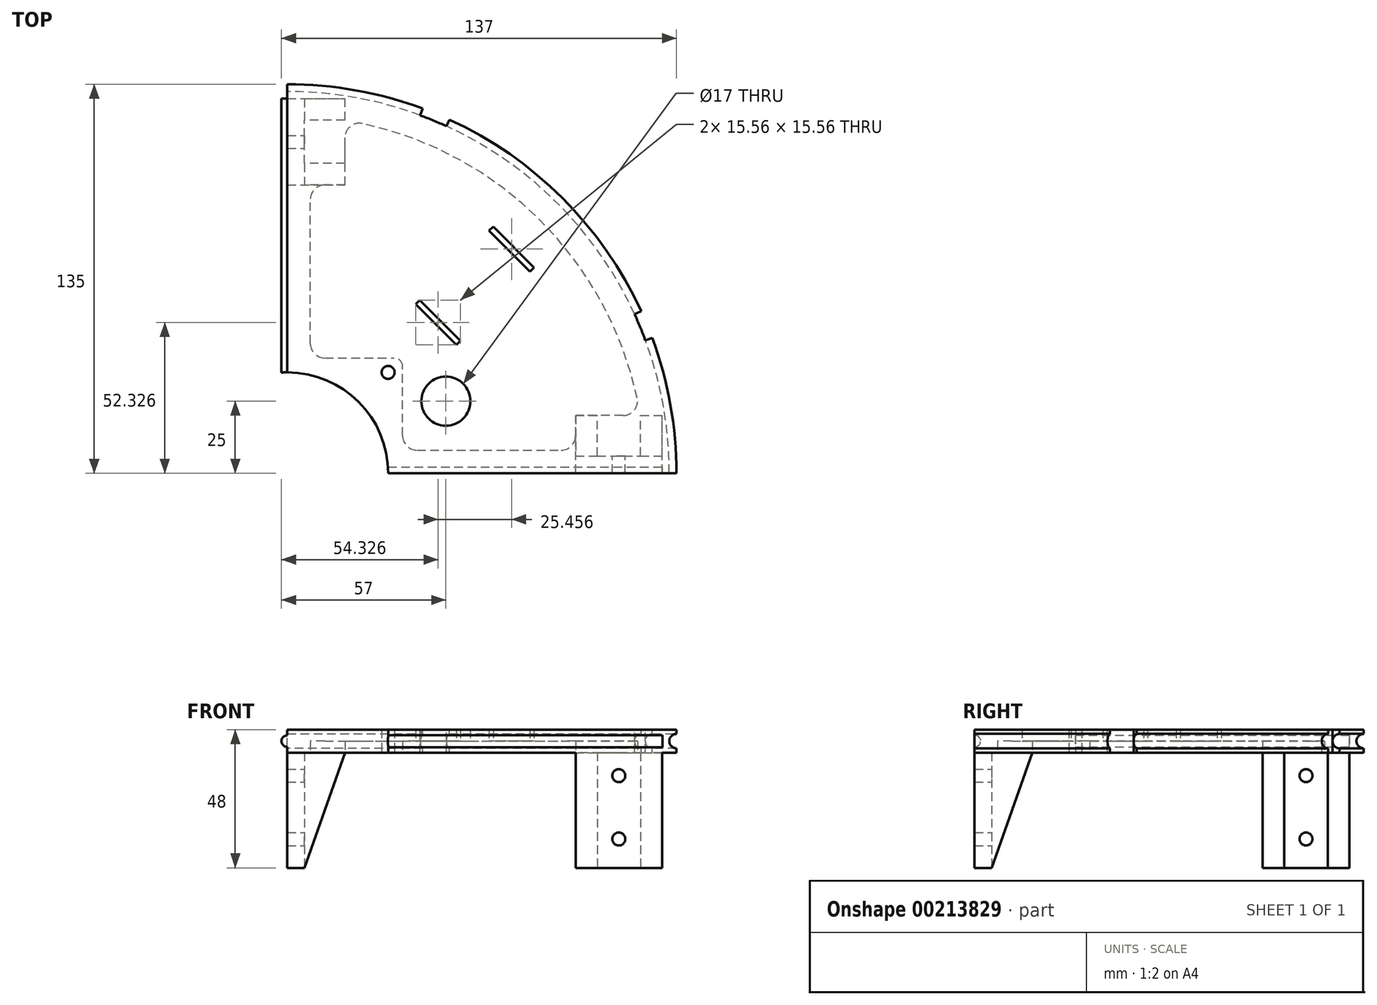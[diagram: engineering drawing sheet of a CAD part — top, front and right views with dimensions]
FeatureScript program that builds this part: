
annotation { "Feature Type Name" : "Feature", "Feature Type Description" : "" }
export const myFeature = defineFeature(function(context is Context, id is Id, definition is map)
    precondition{}
    {
        {
            var Q0;
            Q0=qCreatedBy(makeId("Top.planeOp"),FACE);
            var sketch = newSketch(context, id + "F0", { "sketchPlane" : qUnion([Q0])});
            skArc(sketch, "E0", {"start": v(135, 0) * mm, "mid": v(95.46, 95.46) * mm, "end": v(0, 135) * mm});
            skArc(sketch, "E1", {"start": v(35, 0) * mm, "mid": v(24.75, 24.75) * mm, "end": v(0, 35) * mm});
            skLineSegment(sketch, "E2.trimOffspring", {"start": v(35, 0) * mm, "end": v(135, 0) * mm});
            skLineSegment(sketch, "E3.1.5", {"start": v(0, 35) * mm, "end": v(0, 135) * mm});
            skCircle(sketch, "E4", {"center": v(35, 35) * mm, "radius": 2.25 * mm});
            skSolve(sketch);
        }
        {
            var Q0;
            Q0 = qSketchRegion(id + "F0", true);
            extrude(context, id + "F1", {"entities" : qUnion([Q0]), "depth" : 8 * mm});
        }
        {
            var Q0;
            Q0=qCreatedBy(makeId("Top.planeOp"),FACE);
            cPlane(context, id + "F2", {"entities" : qUnion([Q0]), "cplaneType" : CPlaneType.OFFSET, "offset" : 4 * mm, "width" : 150 * mm, "height" : 150 * mm});
        }
        {
            var Q0;
            Q0=qCreatedBy(id+"F2.planeOp",FACE);
            var sketch = newSketch(context, id + "F3", { "sketchPlane" : qUnion([Q0])});
            skCircle(sketch, "E5", {"center": v(0, 0) * mm, "radius": 135 * mm});
            skSolve(sketch);
        }
        {
            var Q0;
            Q0=makeQuery(id+"F1.opExtrude","SWEPT_FACE",FACE,{"disambiguationData":[OSD([sQuery(id+"F0.wireOp",EDGE,"E2.trimOffspring")])]});
            var sketch = newSketch(context, id + "F4", { "sketchPlane" : qUnion([Q0])});
            skCircle(sketch, "E6", {"center": v(135, 4) * mm, "radius": 2.5 * mm});
            skSolve(sketch);
        }
        {
            var Q0;
            Q0 = qSketchRegion(id + "F4", true);
            var Q1;
            Q1 = qConstructionFilter(qBodyType(qCreatedBy(id + "F3" ,EDGE), BodyType.WIRE), ConstructionObject.NO);
            sweep(context, id + "F5", {"operationType" : NewBodyOperationType.REMOVE, "profiles" : qUnion([Q0]), "path" : qUnion([Q1])});
        }
        {
            var Q0;
            Q0=makeQuery(id+"F1.opExtrude","CAP_FACE",FACE,{"disambiguationData":[OSD([sQuery(id+"F0.wireOp",EDGE,"E0"),sQuery(id+"F0.wireOp",EDGE,"E1"),sQuery(id+"F0.wireOp",EDGE,"E2.trimOffspring"),sQuery(id+"F0.wireOp",EDGE,"E3.1.5"),sQuery(id+"F0.wireOp",EDGE,"E4")])],"isStart":true});
            var sketch = newSketch(context, id + "F6", { "sketchPlane" : qUnion([Q0])});
            skLineSegment(sketch, "E7.bottom", {"start": v(100, 0) * mm, "end": v(130, 0) * mm});
            skLineSegment(sketch, "E7.top", {"start": v(100, -20) * mm, "end": v(130, -20) * mm});
            skLineSegment(sketch, "E7.left", {"start": v(100, 0) * mm, "end": v(100, -20) * mm});
            skLineSegment(sketch, "E7.right", {"start": v(130, 0) * mm, "end": v(130, -20) * mm});
            skLineSegment(sketch, "E8.bottom", {"start": v(0, -100) * mm, "end": v(20, -100) * mm});
            skLineSegment(sketch, "E8.top", {"start": v(0, -130) * mm, "end": v(20, -130) * mm});
            skLineSegment(sketch, "E8.left", {"start": v(0, -100) * mm, "end": v(0, -130) * mm});
            skLineSegment(sketch, "E8.right", {"start": v(20, -100) * mm, "end": v(20, -130) * mm});
            skSolve(sketch);
        }
        {
            var Q0;
            Q0 = qSketchRegion(id + "F6", true);
            extrude(context, id + "F7", {"entities" : qUnion([Q0]), "operationType" : NewBodyOperationType.ADD, "depth" : 40 * mm});
        }
        {
            var Q0;
            Q0=makeQuery(id+"F7.opExtrude","CAP_FACE",FACE,{"disambiguationData":[OSD([sQuery(id+"F6.wireOp",EDGE,"E7.bottom"),sQuery(id+"F6.wireOp",EDGE,"E7.top"),sQuery(id+"F6.wireOp",EDGE,"E7.left"),sQuery(id+"F6.wireOp",EDGE,"E7.right")])],"isStart":false});
            var sketch = newSketch(context, id + "F8", { "sketchPlane" : qUnion([Q0])});
            skLineSegment(sketch, "E9.bottom", {"start": v(107.5, -6) * mm, "end": v(122.5, -6) * mm});
            skLineSegment(sketch, "E9.top", {"start": v(107.5, -20) * mm, "end": v(122.5, -20) * mm});
            skLineSegment(sketch, "E9.left", {"start": v(107.5, -6) * mm, "end": v(107.5, -20) * mm});
            skLineSegment(sketch, "E9.right", {"start": v(122.5, -6) * mm, "end": v(122.5, -20) * mm});
            skLineSegment(sketch, "E10.bottom", {"start": v(20, -107.5) * mm, "end": v(6, -107.5) * mm});
            skLineSegment(sketch, "E10.top", {"start": v(20, -122.5) * mm, "end": v(6, -122.5) * mm});
            skLineSegment(sketch, "E10.left", {"start": v(20, -107.5) * mm, "end": v(20, -122.5) * mm});
            skLineSegment(sketch, "E10.right", {"start": v(6, -107.5) * mm, "end": v(6, -122.5) * mm});
            skSolve(sketch);
        }
        {
            var Q0;
            Q0 = qSketchRegion(id + "F8", true);
            extrude(context, id + "F9", {"entities" : qUnion([Q0]), "operationType" : NewBodyOperationType.REMOVE, "oppositeDirection" : true, "depth" : 40 * mm});
        }
        {
            var Q0;
            {var subQ0=sQuery(id+"F6.wireOp",EDGE,"E7.left");var subQ1=sQuery(id+"F6.wireOp",EDGE,"E7.top");Q0=makeQuery(id+"F9.boolean.opBoolean","SPLIT",EDGE,{"disambiguationData":[TD([makeQuery(id+"F7.opExtrude","SWEPT_FACE",FACE,{"disambiguationData":[OSD([subQ0])]})])],"derivedFrom":makeQuery(id+"F7.opExtrude","CAP_EDGE",EDGE,{"disambiguationData":[OSD([subQ1])],"isStart":false})});}
            var Q1;
            {var subQ0=sQuery(id+"F6.wireOp",EDGE,"E7.right");var subQ1=sQuery(id+"F6.wireOp",EDGE,"E7.top");Q1=makeQuery(id+"F9.boolean.opBoolean","SPLIT",EDGE,{"disambiguationData":[TD([makeQuery(id+"F7.opExtrude","SWEPT_FACE",FACE,{"disambiguationData":[OSD([subQ0])]})])],"derivedFrom":makeQuery(id+"F7.opExtrude","CAP_EDGE",EDGE,{"disambiguationData":[OSD([subQ1])],"isStart":false})});}
            chamfer(context, id + "F10", {"entities" : qUnion([Q0, Q1]), "chamferType" : ChamferType.TWO_OFFSETS, "width1" : 14 * mm, "oppositeDirection" : false, "width2" : 40 * mm, "tangentPropagation" : true});
        }
        {
            var Q0;
            Q0=makeQuery(id+"F9.boolean.opBoolean","COPY",FACE,{"derivedFrom":makeQuery(id+"F9.opExtrude","SWEPT_FACE",FACE,{"disambiguationData":[OSD([sQuery(id+"F8.wireOp",EDGE,"E9.bottom")])]})});
            var sketch = newSketch(context, id + "F11", { "sketchPlane" : qUnion([Q0])});
            skCircle(sketch, "E11", {"center": v(-115, -8) * mm, "radius": 2.25 * mm});
            skCircle(sketch, "E12", {"center": v(-115, -30) * mm, "radius": 2.25 * mm});
            skSolve(sketch);
        }
        {
            var Q0;
            Q0 = qSketchRegion(id + "F11", true);
            extrude(context, id + "F12", {"entities" : qUnion([Q0]), "operationType" : NewBodyOperationType.REMOVE, "oppositeDirection" : true, "depth" : 25 * mm});
        }
        {
            var Q0;
            {var subQ0=sQuery(id+"F6.wireOp",EDGE,"E8.bottom");var subQ1=sQuery(id+"F6.wireOp",EDGE,"E8.right");Q0=makeQuery(id+"F9.boolean.opBoolean","SPLIT",EDGE,{"disambiguationData":[TD([makeQuery(id+"F7.opExtrude","SWEPT_FACE",FACE,{"disambiguationData":[OSD([subQ0])]})])],"derivedFrom":makeQuery(id+"F7.opExtrude","CAP_EDGE",EDGE,{"disambiguationData":[OSD([subQ1])],"isStart":false})});}
            var Q1;
            {var subQ0=sQuery(id+"F6.wireOp",EDGE,"E8.right");var subQ1=sQuery(id+"F6.wireOp",EDGE,"E8.top");Q1=makeQuery(id+"F9.boolean.opBoolean","SPLIT",EDGE,{"disambiguationData":[TD([makeQuery(id+"F7.opExtrude","SWEPT_FACE",FACE,{"disambiguationData":[OSD([subQ1])]})])],"derivedFrom":makeQuery(id+"F7.opExtrude","CAP_EDGE",EDGE,{"disambiguationData":[OSD([subQ0])],"isStart":false})});}
            chamfer(context, id + "F13", {"entities" : qUnion([Q0, Q1]), "chamferType" : ChamferType.TWO_OFFSETS, "width1" : 40 * mm, "oppositeDirection" : false, "width2" : 14 * mm, "tangentPropagation" : true});
        }
        {
            var Q0;
            Q0=makeQuery(id+"F9.boolean.opBoolean","COPY",FACE,{"derivedFrom":makeQuery(id+"F9.opExtrude","SWEPT_FACE",FACE,{"disambiguationData":[OSD([sQuery(id+"F8.wireOp",EDGE,"E10.right")])]})});
            var sketch = newSketch(context, id + "F14", { "sketchPlane" : qUnion([Q0])});
            skCircle(sketch, "E13", {"center": v(115, -30) * mm, "radius": 2.25 * mm});
            skCircle(sketch, "E14", {"center": v(115, -8) * mm, "radius": 2.25 * mm});
            skSolve(sketch);
        }
        {
            var Q0;
            Q0 = qSketchRegion(id + "F14", true);
            extrude(context, id + "F15", {"entities" : qUnion([Q0]), "operationType" : NewBodyOperationType.REMOVE, "oppositeDirection" : true, "depth" : 25 * mm});
        }
        {
            var Q0;
            Q0=makeQuery(id+"F1.opExtrude","CAP_FACE",FACE,{"disambiguationData":[OSD([sQuery(id+"F0.wireOp",EDGE,"E0"),sQuery(id+"F0.wireOp",EDGE,"E1"),sQuery(id+"F0.wireOp",EDGE,"E2.trimOffspring"),sQuery(id+"F0.wireOp",EDGE,"E3.1.5"),sQuery(id+"F0.wireOp",EDGE,"E4")])],"isStart":false});
            var sketch = newSketch(context, id + "F16", { "sketchPlane" : qUnion([Q0])});
            skArc(sketch, "E15", {"start": v(124.2, 46.14) * mm, "mid": v(122.41, 50.71) * mm, "end": v(120.45, 55.2) * mm});
            skArc(sketch, "E16", {"start": v(126.55, 47.01) * mm, "mid": v(124.72, 51.67) * mm, "end": v(122.72, 56.25) * mm});
            skLineSegment(sketch, "E17", {"start": v(0, 0) * mm, "end": v(124.72, 51.66) * mm, "construction": true});
            skLineSegment(sketch, "E18", {"start": v(0, 0) * mm, "end": v(51.66, 124.72) * mm, "construction": true});
            skLineSegment(sketch, "E19", {"start": v(46.13, 124.21) * mm, "end": v(47, 126.55) * mm});
            skLineSegment(sketch, "E20", {"start": v(124.2, 46.14) * mm, "end": v(126.55, 47.01) * mm});
            skLineSegment(sketch, "E21", {"start": v(55.2, 120.45) * mm, "end": v(56.24, 122.73) * mm});
            skLineSegment(sketch, "E22", {"start": v(120.45, 55.2) * mm, "end": v(122.72, 56.25) * mm});
            skArc(sketch, "E23.trimOffspring", {"start": v(56.24, 122.73) * mm, "mid": v(51.66, 124.73) * mm, "end": v(47, 126.55) * mm});
            skArc(sketch, "E24.trimOffspring", {"start": v(55.2, 120.45) * mm, "mid": v(50.7, 122.42) * mm, "end": v(46.13, 124.21) * mm});
            skSolve(sketch);
        }
        {
            var Q0;
            Q0 = qSketchRegion(id + "F16", true);
            extrude(context, id + "F17", {"entities" : qUnion([Q0]), "operationType" : NewBodyOperationType.REMOVE, "oppositeDirection" : true, "depth" : 25 * mm});
        }
        {
            var Q0;
            Q0=makeQuery(id+"F9.boolean.opBoolean","MERGE",FACE,{"derivedFrom":[makeQuery(id+"F1.opExtrude","CAP_FACE",FACE,{"disambiguationData":[OSD([sQuery(id+"F0.wireOp",EDGE,"E0"),sQuery(id+"F0.wireOp",EDGE,"E1"),sQuery(id+"F0.wireOp",EDGE,"E2.trimOffspring"),sQuery(id+"F0.wireOp",EDGE,"E3.1.5"),sQuery(id+"F0.wireOp",EDGE,"E4")])],"isStart":true}),makeQuery(id+"F9.opExtrude","CAP_FACE",FACE,{"disambiguationData":[OSD([sQuery(id+"F8.wireOp",EDGE,"E9.bottom"),sQuery(id+"F8.wireOp",EDGE,"E9.top"),sQuery(id+"F8.wireOp",EDGE,"E9.left"),sQuery(id+"F8.wireOp",EDGE,"E9.right")])],"isStart":false}),makeQuery(id+"F9.opExtrude","CAP_FACE",FACE,{"disambiguationData":[OSD([sQuery(id+"F8.wireOp",EDGE,"E10.bottom"),sQuery(id+"F8.wireOp",EDGE,"E10.top"),sQuery(id+"F8.wireOp",EDGE,"E10.left"),sQuery(id+"F8.wireOp",EDGE,"E10.right")])],"isStart":false})]});
            var sketch = newSketch(context, id + "F18", { "sketchPlane" : qUnion([Q0])});
            skLineSegment(sketch, "E25", {"start": v(0, 0) * mm, "end": v(106.07, -106.07) * mm, "construction": true});
            skLineSegment(sketch, "E26", {"start": v(45.96, -60.1) * mm, "end": v(60.1, -45.96) * mm});
            skLineSegment(sketch, "E27", {"start": v(70, -84.15) * mm, "end": v(84.15, -70) * mm});
            skLineSegment(sketch, "E28", {"start": v(44.55, -58.69) * mm, "end": v(58.69, -44.55) * mm});
            skLineSegment(sketch, "E29", {"start": v(71.42, -85.56) * mm, "end": v(85.56, -71.42) * mm});
            skLineSegment(sketch, "E30", {"start": v(44.55, -58.69) * mm, "end": v(45.96, -60.1) * mm});
            skLineSegment(sketch, "E31", {"start": v(58.69, -44.55) * mm, "end": v(60.1, -45.96) * mm});
            skLineSegment(sketch, "E32", {"start": v(84.15, -70) * mm, "end": v(85.56, -71.42) * mm});
            skLineSegment(sketch, "E33", {"start": v(70, -84.15) * mm, "end": v(71.42, -85.56) * mm});
            skSolve(sketch);
        }
        {
            var Q0;
            Q0 = qSketchRegion(id + "F18", true);
            extrude(context, id + "F19", {"entities" : qUnion([Q0]), "operationType" : NewBodyOperationType.REMOVE, "endBound" : BoundingType.THROUGH_ALL, "oppositeDirection" : true, "depth" : 7.8 * mm});
        }
        {
            var Q0;
            Q0=makeQuery(id+"F7.boolean.opBoolean","MERGE",FACE,{"derivedFrom":[makeQuery(id+"F1.opExtrude","SWEPT_FACE",FACE,{"disambiguationData":[OSD([sQuery(id+"F0.wireOp",EDGE,"E2.trimOffspring")])]}),makeQuery(id+"F7.opExtrude","SWEPT_FACE",FACE,{"disambiguationData":[OSD([sQuery(id+"F6.wireOp",EDGE,"E7.bottom")])]})]});
            var sketch = newSketch(context, id + "F20", { "sketchPlane" : qUnion([Q0])});
            skLineSegment(sketch, "E34", {"start": v(0, 4) * mm, "end": v(130.2, 4) * mm});
            skSolve(sketch);
        }
        {
            var Q0;
            Q0=makeQuery(id+"F7.boolean.opBoolean","MERGE",FACE,{"derivedFrom":[makeQuery(id+"F1.opExtrude","SWEPT_FACE",FACE,{"disambiguationData":[OSD([sQuery(id+"F0.wireOp",EDGE,"E3.1.5")])]}),makeQuery(id+"F7.opExtrude","SWEPT_FACE",FACE,{"disambiguationData":[OSD([sQuery(id+"F6.wireOp",EDGE,"E8.left")])]})]});
            var sketch = newSketch(context, id + "F21", { "sketchPlane" : qUnion([Q0])});
            skLineSegment(sketch, "E35", {"start": v(-130, 4) * mm, "end": v(0, 4) * mm});
            skSolve(sketch);
        }
        {
            var Q0;
            Q0=qCreatedBy(makeId("Front.planeOp"),FACE);
            var sketch = newSketch(context, id + "F22", { "sketchPlane" : qUnion([Q0])});
            skCircle(sketch, "E36", {"center": v(0, 4) * mm, "radius": 2 * mm});
            skSolve(sketch);
        }
        {
            var Q0;
            Q0=makeQuery(id+"F22.imprint","IMPRINT",FACE,{"disambiguationData":[TD([[makeQuery(id+"F22.imprint","IMPRINT",EDGE,{"derivedFrom":sQuery(id+"F22.wireOp",EDGE,"E36")}),1.0]])]});
            var Q1;
            Q1=sQuery(id+"F21.wireOp",EDGE,"E35");
            sweep(context, id + "F23", {"operationType" : NewBodyOperationType.ADD, "profiles" : qUnion([Q0]), "path" : qUnion([Q1])});
        }
        {
            var Q0;
            Q0=makeQuery(id+"F1.opExtrude","CAP_FACE",FACE,{"disambiguationData":[OSD([sQuery(id+"F0.wireOp",EDGE,"E0"),sQuery(id+"F0.wireOp",EDGE,"E1"),sQuery(id+"F0.wireOp",EDGE,"E2.trimOffspring"),sQuery(id+"F0.wireOp",EDGE,"E3.1.5"),sQuery(id+"F0.wireOp",EDGE,"E4")])],"isStart":false});
            var sketch = newSketch(context, id + "F24", { "sketchPlane" : qUnion([Q0])});
            skCircle(sketch, "E37", {"center": v(0, 0) * mm, "radius": 35 * mm});
            skSolve(sketch);
        }
        {
            var Q0;
            {var subQ0=sQuery(id+"F24.wireOp",EDGE,"E37");var subQ1=makeQuery(id+"F24.imprint","INTERSECT",VERTEX,{"derivedFrom":[makeQuery(id+"F1.opExtrude","CAP_EDGE",EDGE,{"disambiguationData":[OSD([sQuery(id+"F0.wireOp",EDGE,"E2.trimOffspring")])],"isStart":false}),subQ0]});Q0=makeQuery(id+"F24.imprint","IMPRINT",FACE,{"disambiguationData":[TD([[makeQuery(id+"F24.imprint","IMPRINT",EDGE,{"disambiguationData":[TD([[subQ1,-1.0]])],"derivedFrom":subQ0}),1.0]])]});}
            extrude(context, id + "F25", {"entities" : qUnion([Q0]), "operationType" : NewBodyOperationType.REMOVE, "endBound" : BoundingType.THROUGH_ALL, "oppositeDirection" : true, "depth" : 25 * mm});
        }
        {
            var Q0;
            Q0=qCreatedBy(makeId("Right.planeOp"),FACE);
            var sketch = newSketch(context, id + "F26", { "sketchPlane" : qUnion([Q0])});
            skCircle(sketch, "E38", {"center": v(0, 4) * mm, "radius": 2.1 * mm});
            skSolve(sketch);
        }
        {
            var Q0;
            Q0=makeQuery(id+"F26.imprint","IMPRINT",FACE,{"disambiguationData":[TD([[makeQuery(id+"F26.imprint","IMPRINT",EDGE,{"derivedFrom":sQuery(id+"F26.wireOp",EDGE,"E38")}),1.0]])]});
            var Q1;
            Q1=sQuery(id+"F20.wireOp",EDGE,"E34");
            sweep(context, id + "F27", {"operationType" : NewBodyOperationType.REMOVE, "profiles" : qUnion([Q0]), "path" : qUnion([Q1])});
        }
        {
            var Q0;
            Q0=makeQuery(id+"F9.boolean.opBoolean","MERGE",FACE,{"derivedFrom":[makeQuery(id+"F1.opExtrude","CAP_FACE",FACE,{"disambiguationData":[OSD([sQuery(id+"F0.wireOp",EDGE,"E0"),sQuery(id+"F0.wireOp",EDGE,"E1"),sQuery(id+"F0.wireOp",EDGE,"E2.trimOffspring"),sQuery(id+"F0.wireOp",EDGE,"E3.1.5"),sQuery(id+"F0.wireOp",EDGE,"E4")])],"isStart":true}),makeQuery(id+"F9.opExtrude","CAP_FACE",FACE,{"disambiguationData":[OSD([sQuery(id+"F8.wireOp",EDGE,"E9.bottom"),sQuery(id+"F8.wireOp",EDGE,"E9.top"),sQuery(id+"F8.wireOp",EDGE,"E9.left"),sQuery(id+"F8.wireOp",EDGE,"E9.right")])],"isStart":false}),makeQuery(id+"F9.opExtrude","CAP_FACE",FACE,{"disambiguationData":[OSD([sQuery(id+"F8.wireOp",EDGE,"E10.bottom"),sQuery(id+"F8.wireOp",EDGE,"E10.top"),sQuery(id+"F8.wireOp",EDGE,"E10.left"),sQuery(id+"F8.wireOp",EDGE,"E10.right")])],"isStart":false})]});
            var sketch = newSketch(context, id + "F28", { "sketchPlane" : qUnion([Q0])});
            skCircle(sketch, "E39", {"center": v(55, -25) * mm, "radius": 8.5 * mm});
            skSolve(sketch);
        }
        {
            var Q0;
            Q0=makeQuery(id+"F28.imprint","IMPRINT",FACE,{"disambiguationData":[TD([[makeQuery(id+"F28.imprint","IMPRINT",EDGE,{"derivedFrom":sQuery(id+"F28.wireOp",EDGE,"E39")}),1.0]])]});
            extrude(context, id + "F29", {"entities" : qUnion([Q0]), "operationType" : NewBodyOperationType.REMOVE, "endBound" : BoundingType.THROUGH_ALL, "oppositeDirection" : true, "depth" : 7.6 * mm});
        }
        {
            var Q0;
            Q0=makeQuery(id+"F9.boolean.opBoolean","MERGE",FACE,{"derivedFrom":[makeQuery(id+"F1.opExtrude","CAP_FACE",FACE,{"disambiguationData":[OSD([sQuery(id+"F0.wireOp",EDGE,"E0"),sQuery(id+"F0.wireOp",EDGE,"E1"),sQuery(id+"F0.wireOp",EDGE,"E2.trimOffspring"),sQuery(id+"F0.wireOp",EDGE,"E3.1.5"),sQuery(id+"F0.wireOp",EDGE,"E4")])],"isStart":true}),makeQuery(id+"F9.opExtrude","CAP_FACE",FACE,{"disambiguationData":[OSD([sQuery(id+"F8.wireOp",EDGE,"E9.bottom"),sQuery(id+"F8.wireOp",EDGE,"E9.top"),sQuery(id+"F8.wireOp",EDGE,"E9.left"),sQuery(id+"F8.wireOp",EDGE,"E9.right")])],"isStart":false}),makeQuery(id+"F9.opExtrude","CAP_FACE",FACE,{"disambiguationData":[OSD([sQuery(id+"F8.wireOp",EDGE,"E10.bottom"),sQuery(id+"F8.wireOp",EDGE,"E10.top"),sQuery(id+"F8.wireOp",EDGE,"E10.left"),sQuery(id+"F8.wireOp",EDGE,"E10.right")])],"isStart":false})]});
            var sketch = newSketch(context, id + "F30", { "sketchPlane" : qUnion([Q0])});
            skLineSegment(sketch, "E40.top", {"start": v(13, -40) * mm, "end": v(37, -40) * mm});
            skLineSegment(sketch, "E40.right", {"start": v(40, -13) * mm, "end": v(40, -37) * mm});
            skArc(sketch, "E41", {"start": v(20, -122.5) * mm, "mid": v(87.77, -87.77) * mm, "end": v(122.5, -20) * mm});
            skLineSegment(sketch, "E42", {"start": v(122.5, -20) * mm, "end": v(100, -20) * mm});
            skLineSegment(sketch, "E43", {"start": v(20, -122.5) * mm, "end": v(20, -100) * mm});
            skLineSegment(sketch, "E44", {"start": v(8, -45) * mm, "end": v(8, -100) * mm});
            skLineSegment(sketch, "E45", {"start": v(8, -100) * mm, "end": v(20, -100) * mm});
            skLineSegment(sketch, "E46", {"start": v(45, -8) * mm, "end": v(100, -8) * mm});
            skLineSegment(sketch, "E47", {"start": v(100, -8) * mm, "end": v(100, -20) * mm});
            skPoint(sketch, "E48.visualSharp", {"position": v(40, -40) * mm});
            skArc(sketch, "E48.filletArc", {"start": v(37, -40) * mm, "mid": v(39.12, -39.12) * mm, "end": v(40, -37) * mm});
            skArc(sketch, "E49.filletArc", {"start": v(13, -40) * mm, "mid": v(9.46, -41.46) * mm, "end": v(8, -45) * mm});
            skArc(sketch, "E50.filletArc", {"start": v(45, -8) * mm, "mid": v(41.46, -9.46) * mm, "end": v(40, -13) * mm});
            skSolve(sketch);
        }
        {
            var Q0;
            Q0 = qSketchRegion(id + "F30", true);
            extrude(context, id + "F31", {"entities" : qUnion([Q0]), "operationType" : NewBodyOperationType.REMOVE, "oppositeDirection" : true, "depth" : 4 * mm});
        }
        {
            var Q0;
            Q0=makeQuery(id+"F31.boolean.opBoolean","COPY",EDGE,{"derivedFrom":makeQuery(id+"F31.opExtrude","SWEPT_EDGE",EDGE,{"disambiguationData":[OSD([sQuery(id+"F6.wireOp",EDGE,"E7.left"),sQuery(id+"F30.wireOp",EDGE,"E46"),sQuery(id+"F30.wireOp",EDGE,"E47")])]})});
            var Q1;
            Q1=makeQuery(id+"F31.boolean.opBoolean","COPY",EDGE,{"derivedFrom":makeQuery(id+"F31.opExtrude","SWEPT_EDGE",EDGE,{"disambiguationData":[OSD([sQuery(id+"F6.wireOp",EDGE,"E8.bottom"),sQuery(id+"F30.wireOp",EDGE,"E44"),sQuery(id+"F30.wireOp",EDGE,"E45")])]})});
            var Q2;
            Q2=makeQuery(id+"F31.boolean.opBoolean","COPY",EDGE,{"derivedFrom":makeQuery(id+"F31.opExtrude","SWEPT_EDGE",EDGE,{"disambiguationData":[OSD([sQuery(id+"F0.wireOp",EDGE,"E0"),sQuery(id+"F0.wireOp",EDGE,"E1"),sQuery(id+"F0.wireOp",EDGE,"E2.trimOffspring"),sQuery(id+"F0.wireOp",EDGE,"E3.1.5"),sQuery(id+"F0.wireOp",EDGE,"E4"),sQuery(id+"F6.wireOp",EDGE,"E8.right"),sQuery(id+"F8.wireOp",EDGE,"E9.bottom"),sQuery(id+"F8.wireOp",EDGE,"E9.top"),sQuery(id+"F8.wireOp",EDGE,"E9.left"),sQuery(id+"F8.wireOp",EDGE,"E9.right"),sQuery(id+"F8.wireOp",EDGE,"E10.bottom"),sQuery(id+"F8.wireOp",EDGE,"E10.top"),sQuery(id+"F8.wireOp",EDGE,"E10.left"),sQuery(id+"F8.wireOp",EDGE,"E10.right"),sQuery(id+"F30.wireOp",EDGE,"E41"),sQuery(id+"F30.wireOp",EDGE,"E43")])]})});
            var Q3;
            Q3=makeQuery(id+"F31.boolean.opBoolean","COPY",EDGE,{"derivedFrom":makeQuery(id+"F31.opExtrude","SWEPT_EDGE",EDGE,{"disambiguationData":[OSD([sQuery(id+"F0.wireOp",EDGE,"E0"),sQuery(id+"F0.wireOp",EDGE,"E1"),sQuery(id+"F0.wireOp",EDGE,"E2.trimOffspring"),sQuery(id+"F0.wireOp",EDGE,"E3.1.5"),sQuery(id+"F0.wireOp",EDGE,"E4"),sQuery(id+"F6.wireOp",EDGE,"E7.top"),sQuery(id+"F8.wireOp",EDGE,"E9.bottom"),sQuery(id+"F8.wireOp",EDGE,"E9.top"),sQuery(id+"F8.wireOp",EDGE,"E9.left"),sQuery(id+"F8.wireOp",EDGE,"E9.right"),sQuery(id+"F8.wireOp",EDGE,"E10.bottom"),sQuery(id+"F8.wireOp",EDGE,"E10.top"),sQuery(id+"F8.wireOp",EDGE,"E10.left"),sQuery(id+"F8.wireOp",EDGE,"E10.right"),sQuery(id+"F30.wireOp",EDGE,"E41"),sQuery(id+"F30.wireOp",EDGE,"E42")])]})});
            fillet(context, id + "F32", {"entities" : qUnion([Q0, Q1, Q2, Q3]), "radius" : 5 * mm, "tangentPropagation" : true, "allowEdgeOverflow" : false});
        }
    });
